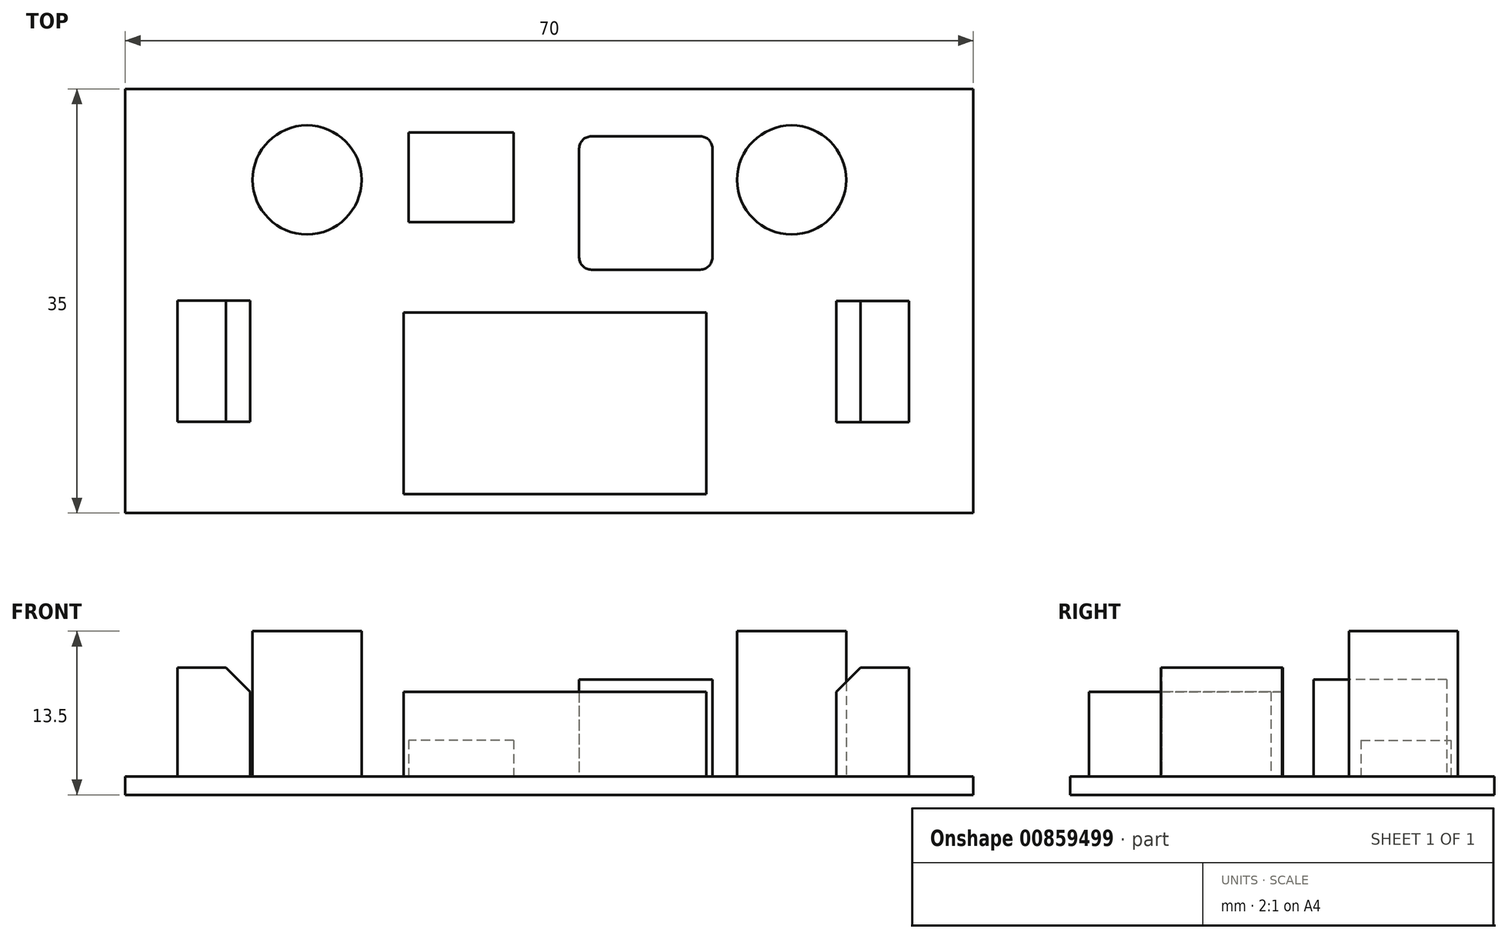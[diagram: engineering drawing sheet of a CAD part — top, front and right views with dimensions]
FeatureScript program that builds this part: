
annotation { "Feature Type Name" : "Feature", "Feature Type Description" : "" }
export const myFeature = defineFeature(function(context is Context, id is Id, definition is map)
    precondition{}
    {
        {
            var Q0;
            Q0=qCreatedBy(makeId("Top.planeOp"),FACE);
            var sketch = newSketch(context, id + "F0", { "sketchPlane" : qUnion([Q0])});
            skLineSegment(sketch, "E0.bottom", {"start": v(35, -17.5) * mm, "end": v(-35, -17.5) * mm});
            skLineSegment(sketch, "E0.top", {"start": v(35, 17.5) * mm, "end": v(-35, 17.5) * mm});
            skLineSegment(sketch, "E0.left", {"start": v(35, -17.5) * mm, "end": v(35, 17.5) * mm});
            skLineSegment(sketch, "E0.right", {"start": v(-35, -17.5) * mm, "end": v(-35, 17.5) * mm});
            skPoint(sketch, "E0.middle", {"position": v(0, 0) * mm});
            skSolve(sketch);
        }
        {
            var Q0;
            Q0=makeQuery(id+"F0.imprint","IMPRINT",FACE,{"disambiguationData":[TD([[makeQuery(id+"F0.imprint","IMPRINT",EDGE,{"derivedFrom":sQuery(id+"F0.wireOp",EDGE,"E0.bottom")}),-1.0]])]});
            extrude(context, id + "F1", {"entities" : qUnion([Q0]), "oppositeDirection" : true, "depth" : 1.5 * mm, "offsetDistance" : 25 * mm});
        }
        {
            var Q0;
            Q0=qCreatedBy(makeId("Top.planeOp"),FACE);
            var sketch = newSketch(context, id + "F2", { "sketchPlane" : qUnion([Q0])});
            skCircle(sketch, "E1", {"center": v(-20, 10) * mm, "radius": 4.5 * mm});
            skCircle(sketch, "E2", {"center": v(20, 10) * mm, "radius": 4.5 * mm});
            skSolve(sketch);
        }
        {
            var Q0;
            Q0=makeQuery(id+"F2.imprint","IMPRINT",FACE,{"disambiguationData":[TD([[makeQuery(id+"F2.imprint","IMPRINT",EDGE,{"derivedFrom":sQuery(id+"F2.wireOp",EDGE,"E1")}),1.0]])]});
            var Q1;
            Q1=makeQuery(id+"F2.imprint","IMPRINT",FACE,{"disambiguationData":[TD([[makeQuery(id+"F2.imprint","IMPRINT",EDGE,{"derivedFrom":sQuery(id+"F2.wireOp",EDGE,"E2")}),1.0]])]});
            var Q2;
            Q2=sQuery(id+"F2.wireOp",EDGE,"E2");
            var Q3;
            Q3=sQuery(id+"F2.wireOp",EDGE,"E1");
            extrude(context, id + "F3", {"entities" : qUnion([Q0, Q1]), "operationType" : NewBodyOperationType.ADD, "surfaceEntities" : qUnion([Q2, Q3]), "depth" : 12 * mm, "offsetDistance" : 25 * mm});
        }
        {
            var Q0;
            Q0=qCreatedBy(makeId("Top.planeOp"),FACE);
            var sketch = newSketch(context, id + "F4", { "sketchPlane" : qUnion([Q0])});
            skLineSegment(sketch, "E3.bottom", {"start": v(-2.94, 6.5) * mm, "end": v(-11.6, 6.5) * mm});
            skLineSegment(sketch, "E3.top", {"start": v(-2.94, 13.92) * mm, "end": v(-11.6, 13.92) * mm});
            skLineSegment(sketch, "E3.left", {"start": v(-2.94, 6.5) * mm, "end": v(-2.94, 13.92) * mm});
            skLineSegment(sketch, "E3.right", {"start": v(-11.6, 6.5) * mm, "end": v(-11.6, 13.92) * mm});
            skPoint(sketch, "E3.middle", {"position": v(-7.27, 10.21) * mm});
            skSolve(sketch);
        }
        {
            var Q0;
            Q0 = qSketchRegion(id + "F4", true);
            extrude(context, id + "F5", {"entities" : qUnion([Q0]), "operationType" : NewBodyOperationType.ADD, "depth" : 3 * mm, "offsetDistance" : 25 * mm});
        }
        {
            var Q0;
            Q0=qCreatedBy(makeId("Top.planeOp"),FACE);
            var sketch = newSketch(context, id + "F6", { "sketchPlane" : qUnion([Q0])});
            skLineSegment(sketch, "E4.bottom", {"start": v(2.46, 13.59) * mm, "end": v(13.46, 13.59) * mm});
            skLineSegment(sketch, "E4.top", {"start": v(2.46, 2.59) * mm, "end": v(13.46, 2.59) * mm});
            skLineSegment(sketch, "E4.left", {"start": v(2.46, 13.59) * mm, "end": v(2.46, 2.59) * mm});
            skLineSegment(sketch, "E4.right", {"start": v(13.46, 13.59) * mm, "end": v(13.46, 2.59) * mm});
            skSolve(sketch);
        }
        {
            var Q0;
            Q0=makeQuery(id+"F6.imprint","IMPRINT",FACE,{"disambiguationData":[TD([[makeQuery(id+"F6.imprint","IMPRINT",EDGE,{"derivedFrom":sQuery(id+"F6.wireOp",EDGE,"E4.bottom")}),-1.0]])]});
            var Q1;
            Q1=sQuery(id+"F6.wireOp",EDGE,"E4.left");
            var Q2;
            Q2=sQuery(id+"F6.wireOp",EDGE,"E4.bottom");
            var Q3;
            Q3=sQuery(id+"F6.wireOp",EDGE,"E4.top");
            var Q4;
            Q4=sQuery(id+"F6.wireOp",EDGE,"E4.right");
            extrude(context, id + "F7", {"entities" : qUnion([Q0]), "operationType" : NewBodyOperationType.ADD, "surfaceEntities" : qUnion([Q1, Q2, Q3, Q4]), "depth" : 8 * mm, "offsetDistance" : 25 * mm});
        }
        {
            var Q0;
            Q0=makeQuery(id+"F7.opExtrude","SWEPT_EDGE",EDGE,{"disambiguationData":[OSD([sQuery(id+"F6.wireOp",EDGE,"E4.bottom"),sQuery(id+"F6.wireOp",EDGE,"E4.right")])]});
            fillet(context, id + "F8", {"entities" : qUnion([Q0]), "radius" : 1 * mm, "tangentPropagation" : true, "allowEdgeOverflow" : false});
        }
        {
            var Q0;
            Q0=makeQuery(id+"F7.opExtrude","SWEPT_EDGE",EDGE,{"disambiguationData":[OSD([sQuery(id+"F6.wireOp",EDGE,"E4.top"),sQuery(id+"F6.wireOp",EDGE,"E4.left")])]});
            var Q1;
            Q1=makeQuery(id+"F7.opExtrude","SWEPT_EDGE",EDGE,{"disambiguationData":[OSD([sQuery(id+"F6.wireOp",EDGE,"E4.top"),sQuery(id+"F6.wireOp",EDGE,"E4.right")])]});
            var Q2;
            Q2=makeQuery(id+"F7.opExtrude","SWEPT_EDGE",EDGE,{"disambiguationData":[OSD([sQuery(id+"F6.wireOp",EDGE,"E4.bottom"),sQuery(id+"F6.wireOp",EDGE,"E4.left")])]});
            fillet(context, id + "F9", {"entities" : qUnion([Q0, Q1, Q2]), "radius" : 1 * mm, "tangentPropagation" : true, "allowEdgeOverflow" : false});
        }
        {
            var Q0;
            Q0=qCreatedBy(makeId("Top.planeOp"),FACE);
            var sketch = newSketch(context, id + "F10", { "sketchPlane" : qUnion([Q0])});
            skLineSegment(sketch, "E5.bottom", {"start": v(-12.04, -0.95) * mm, "end": v(12.96, -0.95) * mm});
            skLineSegment(sketch, "E5.top", {"start": v(-12.04, -15.95) * mm, "end": v(12.96, -15.95) * mm});
            skLineSegment(sketch, "E5.left", {"start": v(-12.04, -0.95) * mm, "end": v(-12.04, -15.95) * mm});
            skLineSegment(sketch, "E5.right", {"start": v(12.96, -0.95) * mm, "end": v(12.96, -15.95) * mm});
            skSolve(sketch);
        }
        {
            var Q0;
            Q0 = qSketchRegion(id + "F10", true);
            extrude(context, id + "F11", {"entities" : qUnion([Q0]), "operationType" : NewBodyOperationType.ADD, "depth" : 7 * mm, "offsetDistance" : 25 * mm});
        }
        {
            var Q0;
            Q0=qCreatedBy(makeId("Top.planeOp"),FACE);
            var sketch = newSketch(context, id + "F12", { "sketchPlane" : qUnion([Q0])});
            skLineSegment(sketch, "E6.bottom", {"start": v(-30.7, 0.05) * mm, "end": v(-24.7, 0.05) * mm});
            skLineSegment(sketch, "E6.top", {"start": v(-30.7, -9.95) * mm, "end": v(-24.7, -9.95) * mm});
            skLineSegment(sketch, "E6.left", {"start": v(-30.7, 0.05) * mm, "end": v(-30.7, -9.95) * mm});
            skLineSegment(sketch, "E6.right", {"start": v(-24.7, 0.05) * mm, "end": v(-24.7, -9.95) * mm});
            skLineSegment(sketch, "E7.bottom", {"start": v(23.7, 0) * mm, "end": v(29.7, 0) * mm});
            skLineSegment(sketch, "E7.top", {"start": v(23.7, -10) * mm, "end": v(29.7, -10) * mm});
            skLineSegment(sketch, "E7.left", {"start": v(23.7, 0) * mm, "end": v(23.7, -10) * mm});
            skLineSegment(sketch, "E7.right", {"start": v(29.7, 0) * mm, "end": v(29.7, -10) * mm});
            skSolve(sketch);
        }
        {
            var Q0;
            Q0=makeQuery(id+"F12.imprint","IMPRINT",FACE,{"disambiguationData":[TD([[makeQuery(id+"F12.imprint","IMPRINT",EDGE,{"derivedFrom":sQuery(id+"F12.wireOp",EDGE,"E7.bottom")}),-1.0]])]});
            var Q1;
            Q1=makeQuery(id+"F12.imprint","IMPRINT",FACE,{"disambiguationData":[TD([[makeQuery(id+"F12.imprint","IMPRINT",EDGE,{"derivedFrom":sQuery(id+"F12.wireOp",EDGE,"E6.bottom")}),-1.0]])]});
            var Q2;
            Q2=sQuery(id+"F12.wireOp",EDGE,"E7.bottom");
            var Q3;
            Q3=sQuery(id+"F12.wireOp",EDGE,"E7.right");
            var Q4;
            Q4=sQuery(id+"F12.wireOp",EDGE,"E7.left");
            var Q5;
            Q5=sQuery(id+"F12.wireOp",EDGE,"E7.top");
            var Q6;
            Q6=sQuery(id+"F12.wireOp",EDGE,"E6.bottom");
            var Q7;
            Q7=sQuery(id+"F12.wireOp",EDGE,"E6.top");
            var Q8;
            Q8=sQuery(id+"F12.wireOp",EDGE,"E6.left");
            var Q9;
            Q9=sQuery(id+"F12.wireOp",EDGE,"E6.right");
            extrude(context, id + "F13", {"entities" : qUnion([Q0, Q1]), "operationType" : NewBodyOperationType.ADD, "surfaceEntities" : qUnion([Q2, Q3, Q4, Q5, Q6, Q7, Q8, Q9]), "depth" : 9 * mm, "offsetDistance" : 25 * mm});
        }
        {
            var Q0;
            Q0=makeQuery(id+"F13.opExtrude","CAP_EDGE",EDGE,{"disambiguationData":[OSD([sQuery(id+"F12.wireOp",EDGE,"E6.right")])],"isStart":false});
            chamfer(context, id + "F14", {"entities" : qUnion([Q0]), "width" : 2 * mm, "tangentPropagation" : true});
        }
        {
            var Q0;
            Q0=makeQuery(id+"F13.opExtrude","CAP_EDGE",EDGE,{"disambiguationData":[OSD([sQuery(id+"F12.wireOp",EDGE,"E7.left")])],"isStart":false});
            chamfer(context, id + "F15", {"entities" : qUnion([Q0]), "width" : 2 * mm, "tangentPropagation" : true});
        }
    });
